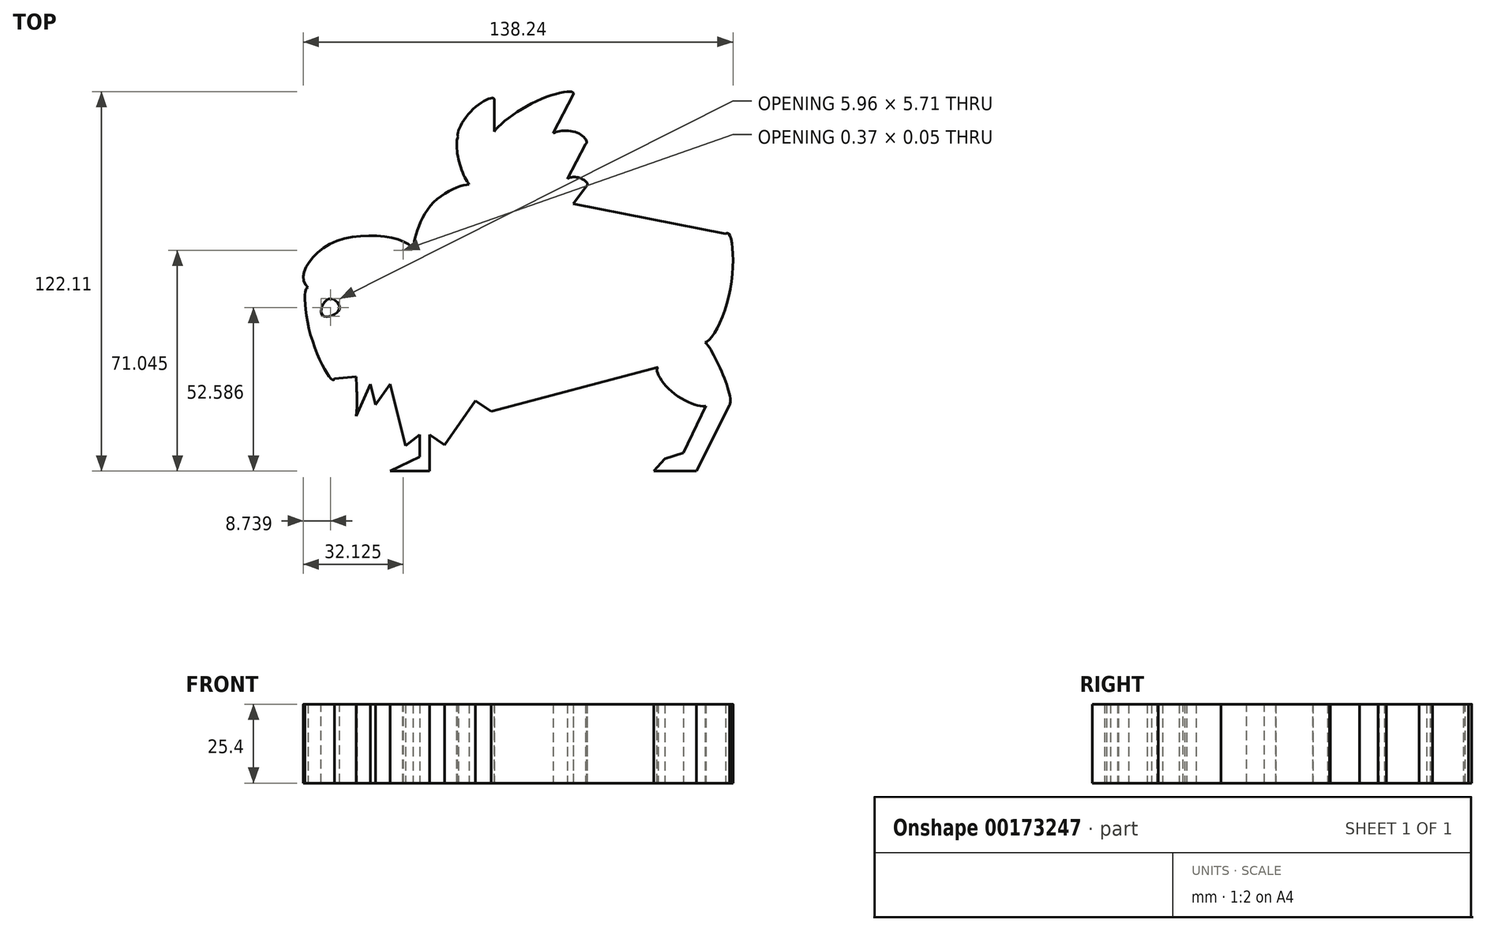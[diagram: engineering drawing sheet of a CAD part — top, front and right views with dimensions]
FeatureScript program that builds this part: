
annotation { "Feature Type Name" : "Feature", "Feature Type Description" : "" }
export const myFeature = defineFeature(function(context is Context, id is Id, definition is map)
    precondition{}
    {
        {
            var Q0;
            Q0=qCreatedBy(makeId("Top.planeOp"),FACE);
            var sketch = newSketch(context, id + "F0", { "sketchPlane" : qUnion([Q0])});
            skLineSegment(sketch, "E0", {"start": v(-58.95, -55.36) * mm, "end": v(-46.25, -55.36) * mm});
            skLineSegment(sketch, "E1", {"start": v(29.53, -55.36) * mm, "end": v(39.6, -55.36) * mm});
            skLineSegment(sketch, "E2", {"start": v(-58.95, -55.36) * mm, "end": v(-49.35, -50.77) * mm});
            skLineSegment(sketch, "E3", {"start": v(-49.35, -50.77) * mm, "end": v(-49.35, -43.67) * mm});
            skLineSegment(sketch, "E4", {"start": v(-49.35, -43.67) * mm, "end": v(-53.94, -47.22) * mm});
            skPoint(sketch, "E4.endSnap0", {"position": v(-49.35, -47.22) * mm});
            skLineSegment(sketch, "E5", {"start": v(-53.94, -47.22) * mm, "end": v(-58.95, -27.4) * mm});
            skLineSegment(sketch, "E6", {"start": v(-58.95, -27.4) * mm, "end": v(-63.54, -34.07) * mm});
            skLineSegment(sketch, "E7", {"start": v(-63.54, -34.07) * mm, "end": v(-65.23, -27.4) * mm});
            skLineSegment(sketch, "E8", {"start": v(-46.25, -55.36) * mm, "end": v(-46.25, -43.67) * mm});
            skLineSegment(sketch, "E9", {"start": v(-46.25, -43.67) * mm, "end": v(-41.42, -47.01) * mm});
            skLineSegment(sketch, "E10", {"start": v(-41.42, -47.01) * mm, "end": v(-31.53, -32.7) * mm});
            skLineSegment(sketch, "E11", {"start": v(-31.53, -32.7) * mm, "end": v(-26.44, -36.22) * mm});
            skLineSegment(sketch, "E12", {"start": v(-26.44, -36.22) * mm, "end": v(27.66, -21.88) * mm});
            skFitSpline(sketch, "E13", {"points": [v(27.66, -21.88) * mm, v(43, -33.67) * mm, v(32.27, -30.26) * mm, v(27.66, -21.88) * mm]});
            skLineSegment(sketch, "E14", {"start": v(43, -33.67) * mm, "end": v(35.44, -49.52) * mm});
            skLineSegment(sketch, "E15", {"start": v(29.53, -51.47) * mm, "end": v(35.44, -49.52) * mm});
            skLineSegment(sketch, "E16", {"start": v(29.53, -51.47) * mm, "end": v(25.93, -55.36) * mm});
            skLineSegment(sketch, "E17", {"start": v(25.93, -55.36) * mm, "end": v(29.53, -55.36) * mm});
            skPoint(sketch, "E18.end.orphan", {"position": v(50.5, -33.67) * mm});
            skLineSegment(sketch, "E19", {"start": v(39.6, -55.36) * mm, "end": v(50.5, -33.67) * mm});
            skFitSpline(sketch, "E20", {"points": [v(50.5, -33.67) * mm, v(41.6, -13.26) * mm, v(43.59, -28.38) * mm, v(50.5, -33.67) * mm]});
            skFitSpline(sketch, "E21", {"points": [v(41.6, -13.26) * mm, v(49, 20.97) * mm, v(49.86, 0) * mm, v(41.6, -13.26) * mm]});
            skLineSegment(sketch, "E22", {"start": v(49, 20.97) * mm, "end": v(0, 30.66) * mm});
            skLineSegment(sketch, "E23", {"start": v(0, 30.66) * mm, "end": v(4.51, 36.65) * mm});
            skFitSpline(sketch, "E24", {"points": [v(4.51, 36.65) * mm, v(-2.9, 36.65) * mm, v(0, 39.22) * mm, v(4.51, 36.65) * mm]});
            skLineSegment(sketch, "E25", {"start": v(-2.9, 36.65) * mm, "end": v(3.94, 49.77) * mm});
            skPoint(sketch, "E26.2.internal.snap0", {"position": v(0.52, 43.21) * mm});
            skFitSpline(sketch, "E27", {"points": [v(3.94, 49.77) * mm, v(-6.9, 52.34) * mm, v(0.52, 53.77) * mm, v(3.94, 49.77) * mm]});
            skLineSegment(sketch, "E28", {"start": v(-6.9, 52.34) * mm, "end": v(0, 65.75) * mm});
            skFitSpline(sketch, "E29", {"points": [v(0, 65.75) * mm, v(-25.41, 52.18) * mm, v(-14, 62.58) * mm, v(0, 65.75) * mm]});
            skLineSegment(sketch, "E30", {"start": v(-25.41, 52.18) * mm, "end": v(-25.41, 64.1) * mm});
            skFitSpline(sketch, "E31", {"points": [v(-25.41, 64.1) * mm, v(-36.57, 52.18) * mm, v(-33.02, 60.3) * mm, v(-25.41, 64.1) * mm]});
            skLineSegment(sketch, "E32", {"start": v(-25.41, 64.1) * mm, "end": v(-25.41, 64.1) * mm});
            skFitSpline(sketch, "E33", {"points": [v(-36.57, 52.18) * mm, v(-32, 36.12) * mm, v(-36.57, 43.56) * mm, v(-36.57, 52.18) * mm]});
            skFitSpline(sketch, "E34", {"points": [v(-32, 36.12) * mm, v(-48.74, 17.94) * mm, v(-51.46, 14.55) * mm, v(-45.58, 30.37) * mm, v(-32, 36.12) * mm]});
            skFitSpline(sketch, "E35", {"points": [v(-51.46, 14.55) * mm, v(-77.22, 18.16) * mm, v(-84.9, 3.48) * mm, v(-51.46, 14.55) * mm]});
            skFitSpline(sketch, "E36", {"points": [v(-84.9, 3.48) * mm, v(-76.76, -25.67) * mm, v(-84.9, -10.08) * mm, v(-84.9, 3.48) * mm]});
            skLineSegment(sketch, "E37", {"start": v(-76.76, -25.67) * mm, "end": v(-69.82, -24.96) * mm});
            skPoint(sketch, "E38.2.internal.orphan", {"position": v(-67.52, -30.74) * mm});
            skPoint(sketch, "E39.end.orphan", {"position": v(-69.82, -34.07) * mm});
            skLineSegment(sketch, "E40", {"start": v(-65.23, -27.4) * mm, "end": v(-69.82, -37.65) * mm});
            skFitSpline(sketch, "E41", {"points": [v(-69.82, -24.96) * mm, v(-69.82, -37.65) * mm, v(-69.82, -39.26) * mm, v(-60.55, -39.48) * mm], "startDerivative": vector(1.33, -34.33) * mm, "endDerivative": vector(32.6, 2) * mm});
            skPoint(sketch, "E42.end.orphan", {"position": v(-78.86, 0) * mm});
            skSolve(sketch);
        }
        {
            var Q0;
            Q0 = qSketchRegion(id + "F0", true);
            extrude(context, id + "F1", {"entities" : qUnion([Q0]), "depth" : 25.4 * mm});
        }
        {
            var Q0;
            Q0=makeQuery(id+"F1.opExtrude","CAP_FACE",FACE,{"disambiguationData":[OSD([sQuery(id+"F0.wireOp",EDGE,"E0"),sQuery(id+"F0.wireOp",EDGE,"E1"),sQuery(id+"F0.wireOp",EDGE,"E2"),sQuery(id+"F0.wireOp",EDGE,"E3"),sQuery(id+"F0.wireOp",EDGE,"E4"),sQuery(id+"F0.wireOp",EDGE,"E5"),sQuery(id+"F0.wireOp",EDGE,"E6"),sQuery(id+"F0.wireOp",EDGE,"E7"),sQuery(id+"F0.wireOp",EDGE,"E8"),sQuery(id+"F0.wireOp",EDGE,"E9"),sQuery(id+"F0.wireOp",EDGE,"E10"),sQuery(id+"F0.wireOp",EDGE,"E11"),sQuery(id+"F0.wireOp",EDGE,"E12"),sQuery(id+"F0.wireOp",EDGE,"E13"),sQuery(id+"F0.wireOp",EDGE,"E14"),sQuery(id+"F0.wireOp",EDGE,"E15"),sQuery(id+"F0.wireOp",EDGE,"E16"),sQuery(id+"F0.wireOp",EDGE,"E17"),sQuery(id+"F0.wireOp",EDGE,"E19"),sQuery(id+"F0.wireOp",EDGE,"E20"),sQuery(id+"F0.wireOp",EDGE,"E21"),sQuery(id+"F0.wireOp",EDGE,"E22"),sQuery(id+"F0.wireOp",EDGE,"E23"),sQuery(id+"F0.wireOp",EDGE,"E24"),sQuery(id+"F0.wireOp",EDGE,"E25"),sQuery(id+"F0.wireOp",EDGE,"E27"),sQuery(id+"F0.wireOp",EDGE,"E28"),sQuery(id+"F0.wireOp",EDGE,"E29"),sQuery(id+"F0.wireOp",EDGE,"E30"),sQuery(id+"F0.wireOp",EDGE,"E31"),sQuery(id+"F0.wireOp",EDGE,"E33"),sQuery(id+"F0.wireOp",EDGE,"E34"),sQuery(id+"F0.wireOp",EDGE,"E35"),sQuery(id+"F0.wireOp",EDGE,"E36"),sQuery(id+"F0.wireOp",EDGE,"E37"),sQuery(id+"F0.wireOp",EDGE,"E40"),sQuery(id+"F0.wireOp",EDGE,"E41")])],"isStart":false});
            var sketch = newSketch(context, id + "F2", { "sketchPlane" : qUnion([Q0])});
            skLineSegment(sketch, "E43", {"start": v(-73.2, 7.52) * mm, "end": v(-73.2, 0) * mm});
            skFitSpline(sketch, "E44", {"points": [v(-73.2, 0) * mm, v(-54.52, 15.7) * mm, v(-63.1, 3.41) * mm, v(-73.2, 0) * mm]});
            skFitSpline(sketch, "E45", {"points": [v(-73.2, 7.52) * mm, v(-54.52, 15.7) * mm, v(-62.36, 10.5) * mm, v(-73.2, 7.52) * mm]});
            skSolve(sketch);
        }
        {
            var Q0;
            {var subQ3=sQuery(id+"F2.wireOp",EDGE,"E45");Q0=makeQuery(id+"F2.imprint","IMPRINT",FACE,{"disambiguationData":[TD([[makeQuery(id+"F2.imprint","IMPRINT",EDGE,{"derivedFrom":subQ3}),1.0]])]});}
            extrude(context, id + "F3", {"entities" : qUnion([Q0]), "operationType" : NewBodyOperationType.REMOVE, "oppositeDirection" : true, "depth" : 25.4 * mm});
        }
        {
            var Q0;
            Q0=makeQuery(id+"F1.opExtrude","CAP_FACE",FACE,{"disambiguationData":[OSD([sQuery(id+"F0.wireOp",EDGE,"E0"),sQuery(id+"F0.wireOp",EDGE,"E1"),sQuery(id+"F0.wireOp",EDGE,"E2"),sQuery(id+"F0.wireOp",EDGE,"E3"),sQuery(id+"F0.wireOp",EDGE,"E4"),sQuery(id+"F0.wireOp",EDGE,"E5"),sQuery(id+"F0.wireOp",EDGE,"E6"),sQuery(id+"F0.wireOp",EDGE,"E7"),sQuery(id+"F0.wireOp",EDGE,"E8"),sQuery(id+"F0.wireOp",EDGE,"E9"),sQuery(id+"F0.wireOp",EDGE,"E10"),sQuery(id+"F0.wireOp",EDGE,"E11"),sQuery(id+"F0.wireOp",EDGE,"E12"),sQuery(id+"F0.wireOp",EDGE,"E13"),sQuery(id+"F0.wireOp",EDGE,"E14"),sQuery(id+"F0.wireOp",EDGE,"E15"),sQuery(id+"F0.wireOp",EDGE,"E16"),sQuery(id+"F0.wireOp",EDGE,"E17"),sQuery(id+"F0.wireOp",EDGE,"E19"),sQuery(id+"F0.wireOp",EDGE,"E20"),sQuery(id+"F0.wireOp",EDGE,"E21"),sQuery(id+"F0.wireOp",EDGE,"E22"),sQuery(id+"F0.wireOp",EDGE,"E23"),sQuery(id+"F0.wireOp",EDGE,"E24"),sQuery(id+"F0.wireOp",EDGE,"E25"),sQuery(id+"F0.wireOp",EDGE,"E27"),sQuery(id+"F0.wireOp",EDGE,"E28"),sQuery(id+"F0.wireOp",EDGE,"E29"),sQuery(id+"F0.wireOp",EDGE,"E30"),sQuery(id+"F0.wireOp",EDGE,"E31"),sQuery(id+"F0.wireOp",EDGE,"E33"),sQuery(id+"F0.wireOp",EDGE,"E34"),sQuery(id+"F0.wireOp",EDGE,"E35"),sQuery(id+"F0.wireOp",EDGE,"E36"),sQuery(id+"F0.wireOp",EDGE,"E37"),sQuery(id+"F0.wireOp",EDGE,"E40"),sQuery(id+"F0.wireOp",EDGE,"E41")])],"isStart":false});
            var sketch = newSketch(context, id + "F4", { "sketchPlane" : qUnion([Q0])});
            skFitSpline(sketch, "E46", {"points": [v(-80.65, -5.27) * mm, v(-75.16, -3.2) * mm, v(-78.73, 0) * mm, v(-80.65, -5.27) * mm]});
            skSolve(sketch);
        }
        {
            var Q0;
            Q0=makeQuery(id+"F4.imprint","IMPRINT",FACE,{"disambiguationData":[TD([[makeQuery(id+"F4.imprint","IMPRINT",EDGE,{"derivedFrom":sQuery(id+"F4.wireOp",EDGE,"E46")}),1.0]])]});
            extrude(context, id + "F5", {"entities" : qUnion([Q0]), "operationType" : NewBodyOperationType.REMOVE, "oppositeDirection" : true, "depth" : 25.4 * mm});
        }
    });
